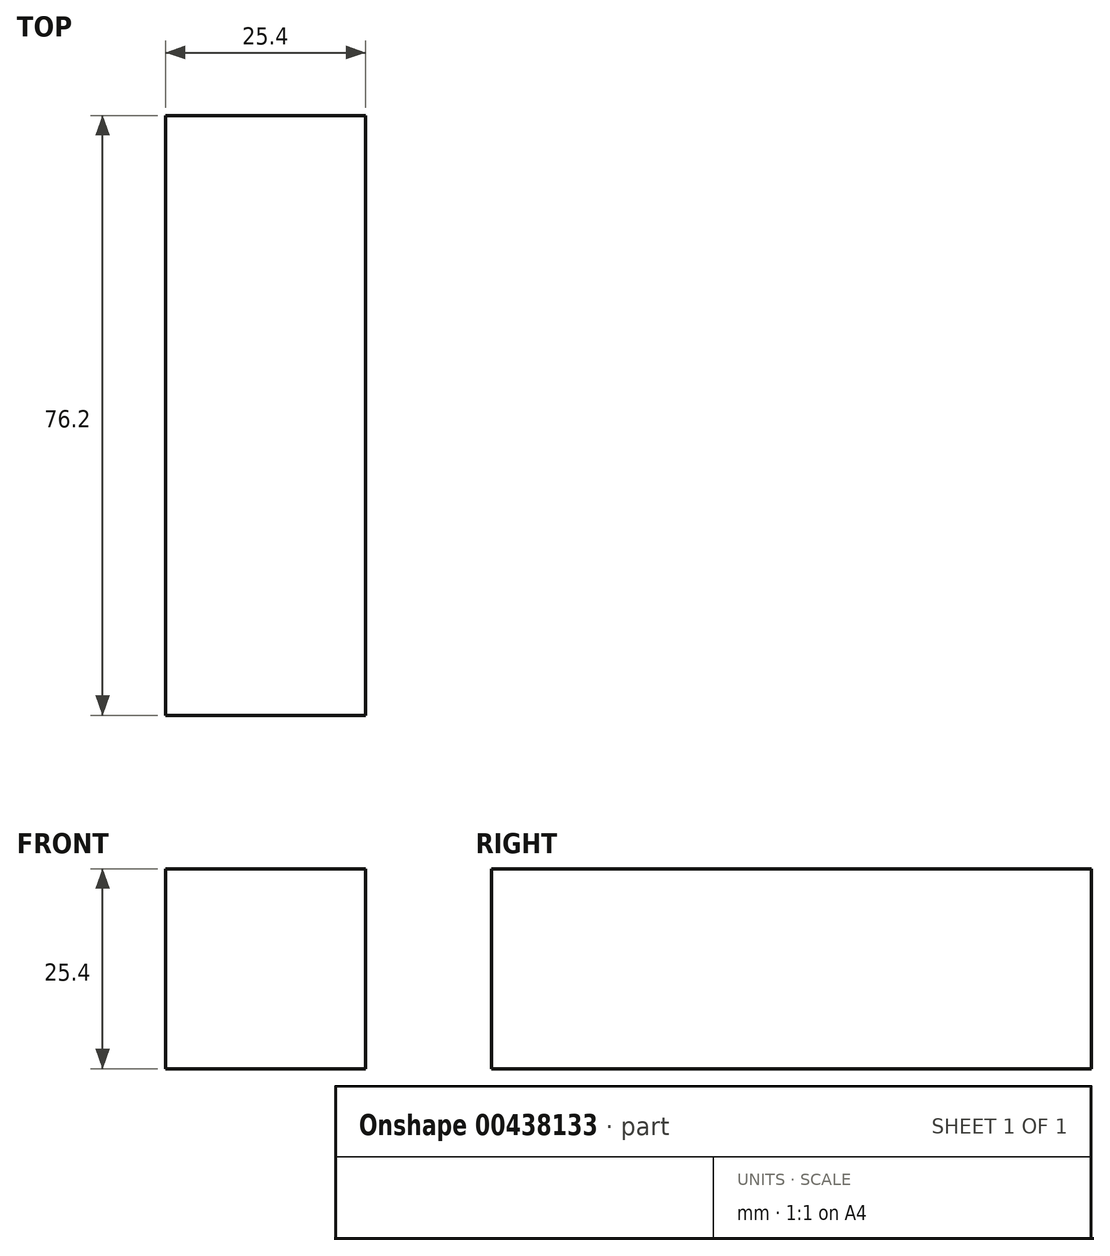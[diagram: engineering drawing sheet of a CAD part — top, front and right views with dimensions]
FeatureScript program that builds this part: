
annotation { "Feature Type Name" : "Feature", "Feature Type Description" : "" }
export const myFeature = defineFeature(function(context is Context, id is Id, definition is map)
    precondition{}
    {
        {
            var Q0;
            Q0=qCreatedBy(makeId("Front.planeOp"),FACE);
            var sketch = newSketch(context, id + "F0", { "sketchPlane" : qUnion([Q0])});
            skLineSegment(sketch, "E0", {"start": v(-59.77, -12.68) * mm, "end": v(-59.77, -38.08) * mm});
            skLineSegment(sketch, "E1", {"start": v(-59.77, -38.08) * mm, "end": v(-34.37, -38.08) * mm});
            skLineSegment(sketch, "E2", {"start": v(-34.37, -38.08) * mm, "end": v(-34.37, -12.68) * mm});
            skLineSegment(sketch, "E3", {"start": v(-34.37, -12.68) * mm, "end": v(-59.77, -12.68) * mm});
            skSolve(sketch);
        }
        {
            var Q0;
            Q0 = qSketchRegion(id + "F0", true);
            extrude(context, id + "F1", {"entities" : qUnion([Q0]), "depth" : 76.2 * mm});
        }
    });
